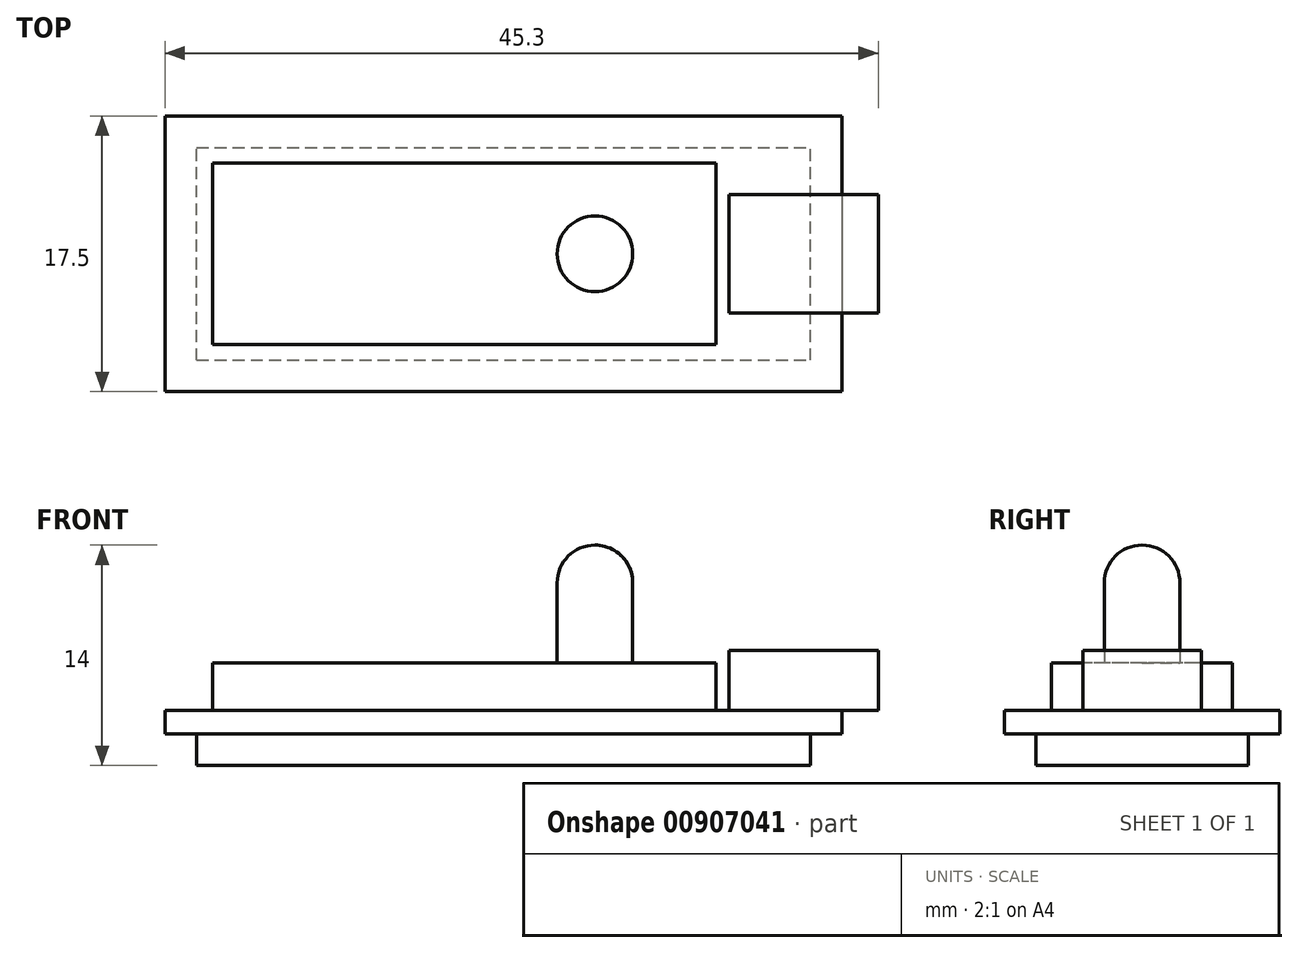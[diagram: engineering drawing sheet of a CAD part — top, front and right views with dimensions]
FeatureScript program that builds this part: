
annotation { "Feature Type Name" : "Feature", "Feature Type Description" : "" }
export const myFeature = defineFeature(function(context is Context, id is Id, definition is map)
    precondition{}
    {
        {
            var Q0;
            Q0=qCreatedBy(makeId("Top.planeOp"),FACE);
            var sketch = newSketch(context, id + "F0", { "sketchPlane" : qUnion([Q0])});
            skLineSegment(sketch, "E0.bottom", {"start": v(-21.5, 8.75) * mm, "end": v(21.5, 8.75) * mm});
            skLineSegment(sketch, "E0.top", {"start": v(-21.5, -8.75) * mm, "end": v(21.5, -8.75) * mm});
            skLineSegment(sketch, "E0.left", {"start": v(-21.5, 8.75) * mm, "end": v(-21.5, -8.75) * mm});
            skLineSegment(sketch, "E0.right", {"start": v(21.5, 8.75) * mm, "end": v(21.5, -8.75) * mm});
            skSolve(sketch);
        }
        {
            var Q0;
            Q0 = qSketchRegion(id + "F0", true);
            extrude(context, id + "F1", {"entities" : qUnion([Q0]), "depth" : 1.5 * mm, "offsetDistance" : 25 * mm});
        }
        {
            var Q0;
            Q0=makeQuery(id+"F1.opExtrude","CAP_FACE",FACE,{"disambiguationData":[OSD([sQuery(id+"F0.wireOp",EDGE,"E0.bottom"),sQuery(id+"F0.wireOp",EDGE,"E0.top"),sQuery(id+"F0.wireOp",EDGE,"E0.left"),sQuery(id+"F0.wireOp",EDGE,"E0.right")])],"isStart":false});
            var sketch = newSketch(context, id + "F2", { "sketchPlane" : qUnion([Q0])});
            skLineSegment(sketch, "E1.bottom", {"start": v(14.3, 3.75) * mm, "end": v(23.8, 3.75) * mm});
            skLineSegment(sketch, "E1.top", {"start": v(14.3, -3.75) * mm, "end": v(23.8, -3.75) * mm});
            skLineSegment(sketch, "E1.left", {"start": v(14.3, 3.75) * mm, "end": v(14.3, -3.75) * mm});
            skLineSegment(sketch, "E1.right", {"start": v(23.8, 3.75) * mm, "end": v(23.8, -3.75) * mm});
            skSolve(sketch);
        }
        {
            var Q0;
            Q0 = qSketchRegion(id + "F2", true);
            extrude(context, id + "F3", {"entities" : qUnion([Q0]), "operationType" : NewBodyOperationType.ADD, "depth" : 3.8 * mm, "offsetDistance" : 25 * mm});
        }
        {
            var Q0;
            Q0=makeQuery(id+"F1.opExtrude","CAP_FACE",FACE,{"disambiguationData":[OSD([sQuery(id+"F0.wireOp",EDGE,"E0.bottom"),sQuery(id+"F0.wireOp",EDGE,"E0.top"),sQuery(id+"F0.wireOp",EDGE,"E0.left"),sQuery(id+"F0.wireOp",EDGE,"E0.right")])],"isStart":false});
            var sketch = newSketch(context, id + "F4", { "sketchPlane" : qUnion([Q0])});
            skLineSegment(sketch, "E2.bottom", {"start": v(-18.5, 5.75) * mm, "end": v(13.5, 5.75) * mm});
            skLineSegment(sketch, "E2.top", {"start": v(-18.5, -5.75) * mm, "end": v(13.5, -5.75) * mm});
            skLineSegment(sketch, "E2.left", {"start": v(-18.5, 5.75) * mm, "end": v(-18.5, -5.75) * mm});
            skLineSegment(sketch, "E2.right", {"start": v(13.5, 5.75) * mm, "end": v(13.5, -5.75) * mm});
            skSolve(sketch);
        }
        {
            var Q0;
            Q0=makeQuery(id+"F4.imprint","IMPRINT",FACE,{"disambiguationData":[TD([[makeQuery(id+"F4.imprint","IMPRINT",EDGE,{"derivedFrom":sQuery(id+"F4.wireOp",EDGE,"E2.bottom")}),-1.0]])]});
            extrude(context, id + "F5", {"entities" : qUnion([Q0]), "operationType" : NewBodyOperationType.ADD, "depth" : 3 * mm, "offsetDistance" : 25 * mm});
        }
        {
            var Q0;
            Q0=makeQuery(id+"F1.opExtrude","CAP_FACE",FACE,{"disambiguationData":[OSD([sQuery(id+"F0.wireOp",EDGE,"E0.bottom"),sQuery(id+"F0.wireOp",EDGE,"E0.top"),sQuery(id+"F0.wireOp",EDGE,"E0.left"),sQuery(id+"F0.wireOp",EDGE,"E0.right")])],"isStart":true});
            var sketch = newSketch(context, id + "F6", { "sketchPlane" : qUnion([Q0])});
            skLineSegment(sketch, "E3.bottom", {"start": v(-19.5, 6.75) * mm, "end": v(19.5, 6.75) * mm});
            skLineSegment(sketch, "E3.top", {"start": v(-19.5, -6.75) * mm, "end": v(19.5, -6.75) * mm});
            skLineSegment(sketch, "E3.left", {"start": v(-19.5, 6.75) * mm, "end": v(-19.5, -6.75) * mm});
            skLineSegment(sketch, "E3.right", {"start": v(19.5, 6.75) * mm, "end": v(19.5, -6.75) * mm});
            skSolve(sketch);
        }
        {
            var Q0;
            Q0=makeQuery(id+"F6.imprint","IMPRINT",FACE,{"disambiguationData":[TD([[makeQuery(id+"F6.imprint","IMPRINT",EDGE,{"derivedFrom":sQuery(id+"F6.wireOp",EDGE,"E3.bottom")}),-1.0]])]});
            extrude(context, id + "F7", {"entities" : qUnion([Q0]), "operationType" : NewBodyOperationType.ADD, "depth" : 2 * mm, "offsetDistance" : 25 * mm});
        }
        {
            var Q0;
            Q0=makeQuery(id+"F5.opExtrude","CAP_FACE",FACE,{"disambiguationData":[OSD([sQuery(id+"F4.wireOp",EDGE,"E2.bottom"),sQuery(id+"F4.wireOp",EDGE,"E2.top"),sQuery(id+"F4.wireOp",EDGE,"E2.left"),sQuery(id+"F4.wireOp",EDGE,"E2.right")])],"isStart":false});
            var sketch = newSketch(context, id + "F8", { "sketchPlane" : qUnion([Q0])});
            skCircle(sketch, "E4", {"center": v(5.8, 0) * mm, "radius": 2.4 * mm});
            skSolve(sketch);
        }
        {
            var Q0;
            Q0=makeQuery(id+"F8.imprint","IMPRINT",FACE,{"disambiguationData":[TD([[makeQuery(id+"F8.imprint","IMPRINT",EDGE,{"derivedFrom":sQuery(id+"F8.wireOp",EDGE,"E4")}),1.0]])]});
            extrude(context, id + "F9", {"entities" : qUnion([Q0]), "operationType" : NewBodyOperationType.ADD, "depth" : 7.5 * mm, "offsetDistance" : 25 * mm});
        }
        {
            var Q0;
            Q0=makeQuery(id+"F9.opExtrude","CAP_EDGE",EDGE,{"disambiguationData":[OSD([sQuery(id+"F8.wireOp",EDGE,"E4")])],"isStart":false});
            fillet(context, id + "F10", {"entities" : qUnion([Q0]), "radius" : 2.4 * mm, "tangentPropagation" : true, "allowEdgeOverflow" : false});
        }
    });
